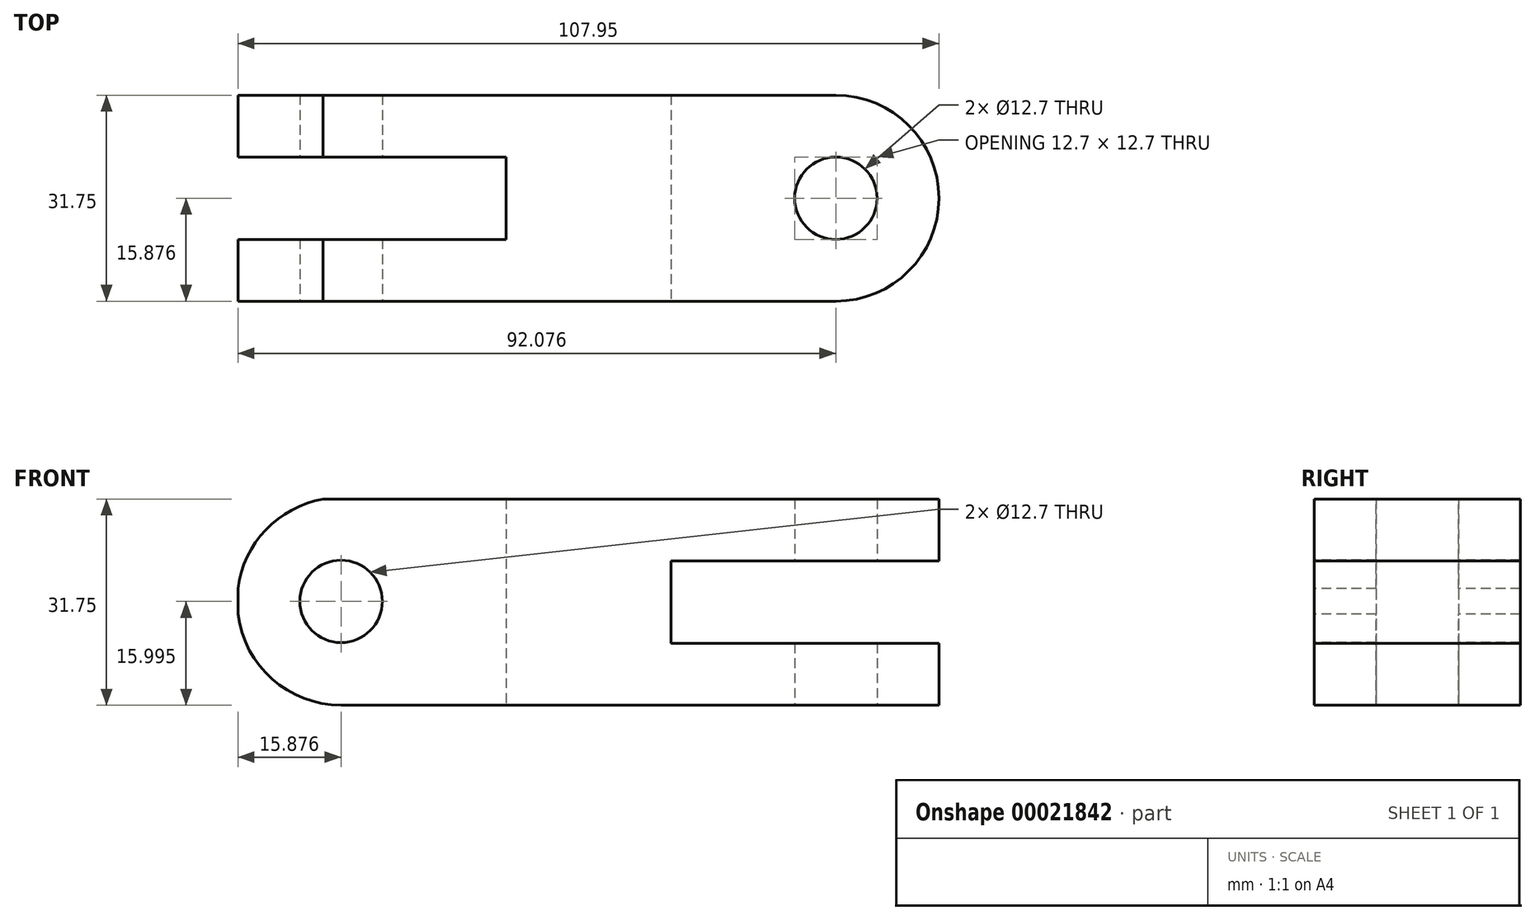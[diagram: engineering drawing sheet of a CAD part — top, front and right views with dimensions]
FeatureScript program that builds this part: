
annotation { "Feature Type Name" : "Feature", "Feature Type Description" : "" }
export const myFeature = defineFeature(function(context is Context, id is Id, definition is map)
    precondition{}
    {
        {
            var Q0;
            Q0=qCreatedBy(makeId("Top.planeOp"),FACE);
            var sketch = newSketch(context, id + "F0", { "sketchPlane" : qUnion([Q0])});
            skLineSegment(sketch, "E0.bottom", {"start": v(-62.89, 29.22) * mm, "end": v(29.19, 29.22) * mm});
            skLineSegment(sketch, "E0.top", {"start": v(-62.89, -2.53) * mm, "end": v(29.19, -2.53) * mm});
            skLineSegment(sketch, "E0.left", {"start": v(-62.89, 29.22) * mm, "end": v(-62.89, 19.7) * mm});
            skLineSegment(sketch, "E0.right", {"start": v(62.13, 12.13) * mm, "end": v(62.13, 12.02) * mm});
            skLineSegment(sketch, "E1.bottom", {"start": v(-62.89, 19.7) * mm, "end": v(-21.61, 19.7) * mm});
            skLineSegment(sketch, "E1.top", {"start": v(-62.89, 7) * mm, "end": v(-21.61, 7) * mm});
            skLineSegment(sketch, "E1.right", {"start": v(-21.61, 19.7) * mm, "end": v(-21.61, 7) * mm});
            skLineSegment(sketch, "E2.trimOffspring", {"start": v(-62.89, 7) * mm, "end": v(-62.89, -2.53) * mm});
            skPoint(sketch, "E3.second.point", {"position": v(29.19, 29.22) * mm});
            skLineSegment(sketch, "E4", {"start": v(-21.61, 13.35) * mm, "end": v(51.37, 13.35) * mm, "construction": true});
            skArc(sketch, "E5", {"start": v(29.19, -2.53) * mm, "mid": v(45.06, 13.35) * mm, "end": v(29.19, 29.22) * mm});
            skCircle(sketch, "E6", {"center": v(29.19, 13.35) * mm, "radius": 6.35 * mm});
            skSolve(sketch);
        }
        {
            var Q0;
            Q0 = qSketchRegion(id + "F0", true);
            extrude(context, id + "F1", {"entities" : qUnion([Q0]), "depth" : 31.75 * mm});
        }
        {
            var Q0;
            Q0=makeQuery(id+"F1.opExtrude","SWEPT_FACE",FACE,{"disambiguationData":[OSD([sQuery(id+"F0.wireOp",EDGE,"E0.top")])]});
            var sketch = newSketch(context, id + "F2", { "sketchPlane" : qUnion([Q0])});
            skLineSegment(sketch, "E7.bottom", {"start": v(-47.01, 0) * mm, "end": v(45.06, 0) * mm});
            skLineSegment(sketch, "E7.top", {"start": v(-47.01, 31.75) * mm, "end": v(45.06, 31.75) * mm});
            skLineSegment(sketch, "E7.right", {"start": v(45.06, 0) * mm, "end": v(45.06, 31.75) * mm});
            skLineSegment(sketch, "E8.0", {"start": v(3.79, 9.53) * mm, "end": v(3.79, 22.22) * mm});
            skLineSegment(sketch, "E9.0", {"start": v(-47.05, 22.22) * mm, "end": v(-45.72, 22.22) * mm});
            skLineSegment(sketch, "E10.0", {"start": v(-47.05, 9.53) * mm, "end": v(-45.72, 9.53) * mm});
            skLineSegment(sketch, "E11.trimOffspring", {"start": v(3.79, 22.22) * mm, "end": v(45.06, 22.22) * mm});
            skLineSegment(sketch, "E12.trimOffspring", {"start": v(3.79, 9.53) * mm, "end": v(45.06, 9.53) * mm});
            skLineSegment(sketch, "E13.0", {"start": v(-47.01, 0) * mm, "end": v(-47.01, 32) * mm, "construction": true});
            skCircle(sketch, "E14", {"center": v(-47.01, 16) * mm, "radius": 6.35 * mm});
            skLineSegment(sketch, "E15", {"start": v(-47.01, 32) * mm, "end": v(-62.89, 31.75) * mm});
            skLineSegment(sketch, "E16", {"start": v(-62.89, 0) * mm, "end": v(-47.01, 0) * mm});
            skLineSegment(sketch, "E17", {"start": v(-62.89, 31.75) * mm, "end": v(-62.89, 0) * mm});
            skArc(sketch, "E18", {"start": v(-44.25, 31.75) * mm, "mid": v(-62.95, 17.38) * mm, "end": v(-47.01, 0) * mm});
            skSolve(sketch);
        }
        {
            var Q0;
            {var subQ0=sQuery(id+"F2.wireOp",EDGE,"E9.0");Q0=makeQuery(id+"F2.imprint","IMPRINT",FACE,{"disambiguationData":[TD([[makeQuery(id+"F2.imprint","IMPRINT",EDGE,{"derivedFrom":subQ0}),-1.0]])]});}
            var Q1;
            {var subQ0=sQuery(id+"F2.wireOp",EDGE,"E10.0");Q1=makeQuery(id+"F2.imprint","IMPRINT",FACE,{"disambiguationData":[TD([[makeQuery(id+"F2.imprint","IMPRINT",EDGE,{"derivedFrom":subQ0}),1.0]])]});}
            var Q2;
            Q2=makeQuery(id+"F2.imprint","IMPRINT",FACE,{"disambiguationData":[TD([[makeQuery(id+"F2.imprint","IMPRINT",EDGE,{"derivedFrom":sQuery(id+"F2.wireOp",EDGE,"28197cf7-9461-44cb-b4fc-d3d9327b2766")}),1.0]])]});
            var Q3;
            {var subQ0=sQuery(id+"F2.wireOp",EDGE,"E9.0");Q3=makeQuery(id+"F2.imprint","IMPRINT",FACE,{"disambiguationData":[TD([[makeQuery(id+"F2.imprint","IMPRINT",EDGE,{"derivedFrom":subQ0}),1.0]])]});}
            var Q4;
            {var subQ0=sQuery(id+"F2.wireOp",EDGE,"E10.0");Q4=makeQuery(id+"F2.imprint","IMPRINT",FACE,{"disambiguationData":[TD([[makeQuery(id+"F2.imprint","IMPRINT",EDGE,{"derivedFrom":subQ0}),-1.0]])]});}
            var Q5;
            {var subQ3=sQuery(id+"F2.wireOp",EDGE,"E11.trimOffspring");var subQ5=sQuery(id+"F2.wireOp",EDGE,"E7.right");var subQ7=makeQuery(id+"F2.imprint","INTERSECT",VERTEX,{"derivedFrom":[subQ5,subQ3]});Q5=makeQuery(id+"F2.imprint","IMPRINT",FACE,{"disambiguationData":[TD([[makeQuery(id+"F2.imprint","IMPRINT",EDGE,{"disambiguationData":[TD([[subQ7,1.0]])],"derivedFrom":subQ5}),1.0]])]});}
            var Q6;
            {var subQ5=sQuery(id+"F2.wireOp",EDGE,"E8.0");Q6=makeQuery(id+"F2.imprint","IMPRINT",FACE,{"disambiguationData":[TD([[makeQuery(id+"F2.imprint","IMPRINT",EDGE,{"derivedFrom":subQ5}),-1.0]])]});}
            var Q7;
            Q7=makeQuery(id+"F2.imprint","IMPRINT",FACE,{"disambiguationData":[TD([[makeQuery(id+"F2.imprint","IMPRINT",EDGE,{"derivedFrom":sQuery(id+"F2.wireOp",EDGE,"E14")}),1.0]])]});
            var Q8;
            {var subQ0=makeQuery(id+"F1.opExtrude","CAP_EDGE",EDGE,{"disambiguationData":[OSD([sQuery(id+"F0.wireOp",EDGE,"E0.top")])],"isStart":false});var subQ3=sQuery(id+"F2.wireOp",EDGE,"d61c9fb1-0ed8-42f5-90a1-883d1494d07f");var subQ4=makeQuery(id+"F2.imprint","INTERSECT",VERTEX,{"derivedFrom":[subQ0,subQ3]});Q8=makeQuery(id+"F2.imprint","IMPRINT",FACE,{"disambiguationData":[TD([[makeQuery(id+"F2.imprint","IMPRINT",EDGE,{"disambiguationData":[TD([[subQ4,-1.0]])],"derivedFrom":subQ3}),1.0]])]});}
            var Q9;
            {var subQ0=makeQuery(id+"F1.opExtrude","CAP_EDGE",EDGE,{"disambiguationData":[OSD([sQuery(id+"F0.wireOp",EDGE,"E0.top")])],"isStart":false});var subQ3=sQuery(id+"F2.wireOp",EDGE,"E17");var subQ4=makeQuery(id+"F2.imprint","INTERSECT",VERTEX,{"derivedFrom":[subQ0,subQ3]});Q9=makeQuery(id+"F2.imprint","IMPRINT",FACE,{"disambiguationData":[TD([[makeQuery(id+"F2.imprint","IMPRINT",EDGE,{"disambiguationData":[TD([[subQ4,-1.0]])],"derivedFrom":subQ3}),1.0]])]});}
            var Q10;
            {var subQ3=sQuery(id+"F2.wireOp",EDGE,"E16");Q10=makeQuery(id+"F2.imprint","IMPRINT",FACE,{"disambiguationData":[TD([[makeQuery(id+"F2.imprint","IMPRINT",EDGE,{"derivedFrom":subQ3}),1.0]])]});}
            extrude(context, id + "F3", {"entities" : qUnion([Q0, Q1, Q2, Q3, Q4, Q5, Q6, Q7, Q8, Q9, Q10]), "operationType" : NewBodyOperationType.REMOVE, "endBound" : BoundingType.THROUGH_ALL, "oppositeDirection" : true, "depth" : 25.4 * mm});
        }
    });
